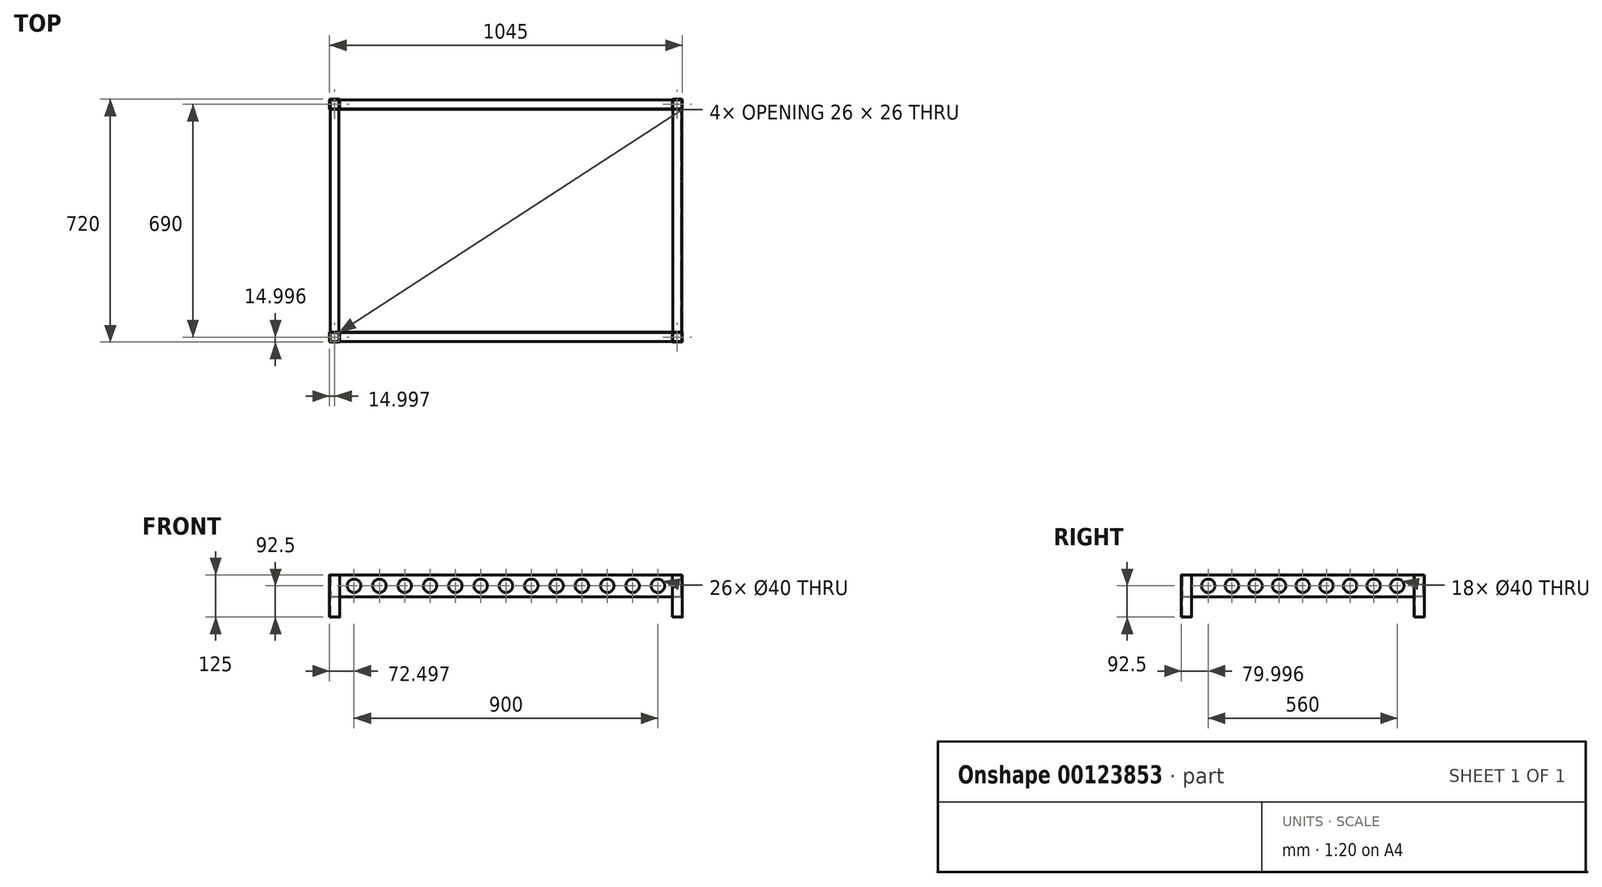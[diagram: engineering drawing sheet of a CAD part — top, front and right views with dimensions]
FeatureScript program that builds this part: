
annotation { "Feature Type Name" : "Feature", "Feature Type Description" : "" }
export const myFeature = defineFeature(function(context is Context, id is Id, definition is map)
    precondition{}
    {
        {
            var Q0;
            Q0=qCreatedBy(makeId("Top.planeOp"),FACE);
            var sketch = newSketch(context, id + "F0", { "sketchPlane" : qUnion([Q0])});
            skLineSegment(sketch, "E0.bottom", {"start": v(-74.45, 26.98) * mm, "end": v(-100.45, 26.98) * mm});
            skLineSegment(sketch, "E0.top", {"start": v(-74.45, 56.98) * mm, "end": v(-100.45, 56.98) * mm});
            skLineSegment(sketch, "E0.left", {"start": v(-72.45, 28.98) * mm, "end": v(-72.45, 54.98) * mm});
            skLineSegment(sketch, "E0.right", {"start": v(-102.45, 28.98) * mm, "end": v(-102.45, 54.98) * mm});
            skPoint(sketch, "E0.middle", {"position": v(-87.45, 41.98) * mm});
            skLineSegment(sketch, "E1.bottom", {"start": v(-75.45, 28.98) * mm, "end": v(-99.45, 28.98) * mm});
            skLineSegment(sketch, "E1.top", {"start": v(-75.45, 54.98) * mm, "end": v(-99.45, 54.98) * mm});
            skLineSegment(sketch, "E1.left", {"start": v(-74.45, 29.98) * mm, "end": v(-74.45, 53.98) * mm});
            skLineSegment(sketch, "E1.right", {"start": v(-100.45, 29.98) * mm, "end": v(-100.45, 53.98) * mm});
            skPoint(sketch, "E2.visualSharp", {"position": v(-102.45, 56.98) * mm});
            skArc(sketch, "E2.filletArc", {"start": v(-100.45, 56.98) * mm, "mid": v(-101.87, 56.39) * mm, "end": v(-102.45, 54.98) * mm});
            skPoint(sketch, "E3.visualSharp", {"position": v(-102.45, 26.98) * mm});
            skArc(sketch, "E3.filletArc", {"start": v(-102.45, 28.98) * mm, "mid": v(-101.87, 27.56) * mm, "end": v(-100.45, 26.98) * mm});
            skPoint(sketch, "E4.visualSharp", {"position": v(-72.45, 26.98) * mm});
            skArc(sketch, "E4.filletArc", {"start": v(-74.45, 26.98) * mm, "mid": v(-73.04, 27.56) * mm, "end": v(-72.45, 28.98) * mm});
            skPoint(sketch, "E5.visualSharp", {"position": v(-72.45, 56.98) * mm});
            skArc(sketch, "E5.filletArc", {"start": v(-72.45, 54.98) * mm, "mid": v(-73.04, 56.39) * mm, "end": v(-74.45, 56.98) * mm});
            skArc(sketch, "E6.filletArc", {"start": v(-74.45, 53.98) * mm, "mid": v(-74.75, 54.68) * mm, "end": v(-75.45, 54.98) * mm});
            skArc(sketch, "E7.filletArc", {"start": v(-99.45, 54.98) * mm, "mid": v(-100.16, 54.68) * mm, "end": v(-100.45, 53.98) * mm});
            skArc(sketch, "E8.filletArc", {"start": v(-100.45, 29.98) * mm, "mid": v(-100.16, 29.27) * mm, "end": v(-99.45, 28.98) * mm});
            skArc(sketch, "E9.filletArc", {"start": v(-75.45, 28.98) * mm, "mid": v(-74.75, 29.27) * mm, "end": v(-74.45, 29.98) * mm});
            skPoint(sketch, "E10.0.1.0", {"position": v(-72.45, -633.02) * mm});
            skPoint(sketch, "E10.0.1.1", {"position": v(-74.45, -635.02) * mm});
            skPoint(sketch, "E10.0.1.2", {"position": v(-74.45, -661.02) * mm});
            skPoint(sketch, "E10.0.1.3", {"position": v(-72.45, -663.02) * mm});
            skPoint(sketch, "E10.0.1.4", {"position": v(-87.45, -648.02) * mm});
            skLineSegment(sketch, "E10.0.1.5", {"start": v(-74.45, -663.02) * mm, "end": v(-100.45, -663.02) * mm});
            skLineSegment(sketch, "E10.0.1.6", {"start": v(-74.45, -633.02) * mm, "end": v(-100.45, -633.02) * mm});
            skPoint(sketch, "E10.0.1.7", {"position": v(-102.45, -663.02) * mm});
            skLineSegment(sketch, "E10.0.1.8", {"start": v(-74.45, -660.02) * mm, "end": v(-74.45, -636.02) * mm});
            skPoint(sketch, "E10.0.1.9", {"position": v(-100.45, -635.02) * mm});
            skArc(sketch, "E10.0.1.10", {"start": v(-100.45, -633.02) * mm, "mid": v(-101.87, -633.61) * mm, "end": v(-102.45, -635.02) * mm});
            skLineSegment(sketch, "E10.0.1.11", {"start": v(-75.45, -635.02) * mm, "end": v(-99.45, -635.02) * mm});
            skLineSegment(sketch, "E10.0.1.12", {"start": v(-72.45, -661.02) * mm, "end": v(-72.45, -635.02) * mm});
            skLineSegment(sketch, "E10.0.1.13", {"start": v(-75.45, -661.02) * mm, "end": v(-99.45, -661.02) * mm});
            skPoint(sketch, "E10.0.1.14", {"position": v(-102.45, -633.02) * mm});
            skLineSegment(sketch, "E10.0.1.15", {"start": v(-102.45, -661.02) * mm, "end": v(-102.45, -635.02) * mm});
            skLineSegment(sketch, "E10.0.1.16", {"start": v(-100.45, -660.02) * mm, "end": v(-100.45, -636.02) * mm});
            skArc(sketch, "E10.0.1.17", {"start": v(-72.45, -635.02) * mm, "mid": v(-73.04, -633.61) * mm, "end": v(-74.45, -633.02) * mm});
            skPoint(sketch, "E10.0.1.18", {"position": v(-100.45, -661.02) * mm});
            skArc(sketch, "E10.0.1.19", {"start": v(-102.45, -661.02) * mm, "mid": v(-101.87, -662.44) * mm, "end": v(-100.45, -663.02) * mm});
            skPoint(sketch, "E10.0.1.20", {"position": v(-87.45, -648.02) * mm});
            skArc(sketch, "E10.0.1.21", {"start": v(-74.45, -663.02) * mm, "mid": v(-73.04, -662.44) * mm, "end": v(-72.45, -661.02) * mm});
            skArc(sketch, "E10.0.1.22", {"start": v(-75.45, -661.02) * mm, "mid": v(-74.75, -660.73) * mm, "end": v(-74.45, -660.02) * mm});
            skArc(sketch, "E10.0.1.23", {"start": v(-100.45, -660.02) * mm, "mid": v(-100.16, -660.73) * mm, "end": v(-99.45, -661.02) * mm});
            skArc(sketch, "E10.0.1.24", {"start": v(-99.45, -635.02) * mm, "mid": v(-100.16, -635.32) * mm, "end": v(-100.45, -636.02) * mm});
            skArc(sketch, "E10.0.1.25", {"start": v(-74.45, -636.02) * mm, "mid": v(-74.75, -635.32) * mm, "end": v(-75.45, -635.02) * mm});
            skPoint(sketch, "E10.1.0.0", {"position": v(942.55, 56.98) * mm});
            skPoint(sketch, "E10.1.0.1", {"position": v(940.55, 54.98) * mm});
            skPoint(sketch, "E10.1.0.2", {"position": v(940.55, 28.98) * mm});
            skPoint(sketch, "E10.1.0.3", {"position": v(942.55, 26.98) * mm});
            skPoint(sketch, "E10.1.0.4", {"position": v(927.55, 41.98) * mm});
            skLineSegment(sketch, "E10.1.0.5", {"start": v(940.55, 26.98) * mm, "end": v(914.55, 26.98) * mm});
            skLineSegment(sketch, "E10.1.0.6", {"start": v(940.55, 56.98) * mm, "end": v(914.55, 56.98) * mm});
            skPoint(sketch, "E10.1.0.7", {"position": v(912.55, 26.98) * mm});
            skLineSegment(sketch, "E10.1.0.8", {"start": v(940.55, 29.98) * mm, "end": v(940.55, 53.98) * mm});
            skPoint(sketch, "E10.1.0.9", {"position": v(914.55, 54.98) * mm});
            skArc(sketch, "E10.1.0.10", {"start": v(914.55, 56.98) * mm, "mid": v(913.13, 56.39) * mm, "end": v(912.55, 54.98) * mm});
            skLineSegment(sketch, "E10.1.0.11", {"start": v(939.55, 54.98) * mm, "end": v(915.55, 54.98) * mm});
            skLineSegment(sketch, "E10.1.0.12", {"start": v(942.55, 28.98) * mm, "end": v(942.55, 54.98) * mm});
            skLineSegment(sketch, "E10.1.0.13", {"start": v(939.55, 28.98) * mm, "end": v(915.55, 28.98) * mm});
            skPoint(sketch, "E10.1.0.14", {"position": v(912.55, 56.98) * mm});
            skLineSegment(sketch, "E10.1.0.15", {"start": v(912.55, 28.98) * mm, "end": v(912.55, 54.98) * mm});
            skLineSegment(sketch, "E10.1.0.16", {"start": v(914.55, 29.98) * mm, "end": v(914.55, 53.98) * mm});
            skArc(sketch, "E10.1.0.17", {"start": v(942.55, 54.98) * mm, "mid": v(941.96, 56.39) * mm, "end": v(940.55, 56.98) * mm});
            skPoint(sketch, "E10.1.0.18", {"position": v(914.55, 28.98) * mm});
            skArc(sketch, "E10.1.0.19", {"start": v(912.55, 28.98) * mm, "mid": v(913.13, 27.56) * mm, "end": v(914.55, 26.98) * mm});
            skPoint(sketch, "E10.1.0.20", {"position": v(927.55, 41.98) * mm});
            skArc(sketch, "E10.1.0.21", {"start": v(940.55, 26.98) * mm, "mid": v(941.96, 27.56) * mm, "end": v(942.55, 28.98) * mm});
            skArc(sketch, "E10.1.0.22", {"start": v(939.55, 28.98) * mm, "mid": v(940.25, 29.27) * mm, "end": v(940.55, 29.98) * mm});
            skArc(sketch, "E10.1.0.23", {"start": v(914.55, 29.98) * mm, "mid": v(914.84, 29.27) * mm, "end": v(915.55, 28.98) * mm});
            skArc(sketch, "E10.1.0.24", {"start": v(915.55, 54.98) * mm, "mid": v(914.84, 54.68) * mm, "end": v(914.55, 53.98) * mm});
            skArc(sketch, "E10.1.0.25", {"start": v(940.55, 53.98) * mm, "mid": v(940.25, 54.68) * mm, "end": v(939.55, 54.98) * mm});
            skPoint(sketch, "E10.1.1.0", {"position": v(942.55, -633.02) * mm});
            skPoint(sketch, "E10.1.1.1", {"position": v(940.55, -635.02) * mm});
            skPoint(sketch, "E10.1.1.2", {"position": v(940.55, -661.02) * mm});
            skPoint(sketch, "E10.1.1.3", {"position": v(942.55, -663.02) * mm});
            skPoint(sketch, "E10.1.1.4", {"position": v(927.55, -648.02) * mm});
            skLineSegment(sketch, "E10.1.1.5", {"start": v(940.55, -663.02) * mm, "end": v(914.55, -663.02) * mm});
            skLineSegment(sketch, "E10.1.1.6", {"start": v(940.55, -633.02) * mm, "end": v(914.55, -633.02) * mm});
            skPoint(sketch, "E10.1.1.7", {"position": v(912.55, -663.02) * mm});
            skLineSegment(sketch, "E10.1.1.8", {"start": v(940.55, -660.02) * mm, "end": v(940.55, -636.02) * mm});
            skPoint(sketch, "E10.1.1.9", {"position": v(914.55, -635.02) * mm});
            skArc(sketch, "E10.1.1.10", {"start": v(914.55, -633.02) * mm, "mid": v(913.13, -633.61) * mm, "end": v(912.55, -635.02) * mm});
            skLineSegment(sketch, "E10.1.1.11", {"start": v(939.55, -635.02) * mm, "end": v(915.55, -635.02) * mm});
            skLineSegment(sketch, "E10.1.1.12", {"start": v(942.55, -661.02) * mm, "end": v(942.55, -635.02) * mm});
            skLineSegment(sketch, "E10.1.1.13", {"start": v(939.55, -661.02) * mm, "end": v(915.55, -661.02) * mm});
            skPoint(sketch, "E10.1.1.14", {"position": v(912.55, -633.02) * mm});
            skLineSegment(sketch, "E10.1.1.15", {"start": v(912.55, -661.02) * mm, "end": v(912.55, -635.02) * mm});
            skLineSegment(sketch, "E10.1.1.16", {"start": v(914.55, -660.02) * mm, "end": v(914.55, -636.02) * mm});
            skArc(sketch, "E10.1.1.17", {"start": v(942.55, -635.02) * mm, "mid": v(941.96, -633.61) * mm, "end": v(940.55, -633.02) * mm});
            skPoint(sketch, "E10.1.1.18", {"position": v(914.55, -661.02) * mm});
            skArc(sketch, "E10.1.1.19", {"start": v(912.55, -661.02) * mm, "mid": v(913.13, -662.44) * mm, "end": v(914.55, -663.02) * mm});
            skPoint(sketch, "E10.1.1.20", {"position": v(927.55, -648.02) * mm});
            skArc(sketch, "E10.1.1.21", {"start": v(940.55, -663.02) * mm, "mid": v(941.96, -662.44) * mm, "end": v(942.55, -661.02) * mm});
            skArc(sketch, "E10.1.1.22", {"start": v(939.55, -661.02) * mm, "mid": v(940.25, -660.73) * mm, "end": v(940.55, -660.02) * mm});
            skArc(sketch, "E10.1.1.23", {"start": v(914.55, -660.02) * mm, "mid": v(914.84, -660.73) * mm, "end": v(915.55, -661.02) * mm});
            skArc(sketch, "E10.1.1.24", {"start": v(915.55, -635.02) * mm, "mid": v(914.84, -635.32) * mm, "end": v(914.55, -636.02) * mm});
            skArc(sketch, "E10.1.1.25", {"start": v(940.55, -636.02) * mm, "mid": v(940.25, -635.32) * mm, "end": v(939.55, -635.02) * mm});
            skLineSegment(sketch, "E10.direction1", {"start": v(-102.45, 26.98) * mm, "end": v(912.55, 26.98) * mm, "construction": true});
            skLineSegment(sketch, "E10.direction2", {"start": v(-102.45, 26.98) * mm, "end": v(-102.45, -663.02) * mm, "construction": true});
            skSolve(sketch);
        }
        {
            var Q0;
            Q0=makeQuery(id+"F0.imprint","IMPRINT",FACE,{"disambiguationData":[TD([[makeQuery(id+"F0.imprint","IMPRINT",EDGE,{"derivedFrom":sQuery(id+"F0.wireOp",EDGE,"E0.bottom")}),-1.0]])]});
            var Q1;
            Q1=makeQuery(id+"F0.imprint","IMPRINT",FACE,{"disambiguationData":[TD([[makeQuery(id+"F0.imprint","IMPRINT",EDGE,{"derivedFrom":sQuery(id+"F0.wireOp",EDGE,"E10.0.1.5")}),-1.0]])]});
            var Q2;
            Q2=makeQuery(id+"F0.imprint","IMPRINT",FACE,{"disambiguationData":[TD([[makeQuery(id+"F0.imprint","IMPRINT",EDGE,{"derivedFrom":sQuery(id+"F0.wireOp",EDGE,"E10.1.1.5")}),-1.0]])]});
            var Q3;
            Q3=makeQuery(id+"F0.imprint","IMPRINT",FACE,{"disambiguationData":[TD([[makeQuery(id+"F0.imprint","IMPRINT",EDGE,{"derivedFrom":sQuery(id+"F0.wireOp",EDGE,"E10.1.0.5")}),-1.0]])]});
            extrude(context, id + "F1", {"entities" : qUnion([Q0, Q1, Q2, Q3]), "depth" : 125 * mm});
        }
        {
            var Q0;
            Q0=makeQuery(id+"F1.opExtrude","SWEPT_FACE",FACE,{"disambiguationData":[OSD([sQuery(id+"F0.wireOp",EDGE,"E0.bottom")])]});
            var sketch = newSketch(context, id + "F2", { "sketchPlane" : qUnion([Q0])});
            skLineSegment(sketch, "E11", {"start": v(-74.45, 125) * mm, "end": v(-99.45, 125) * mm});
            skLineSegment(sketch, "E12", {"start": v(-100.45, 124) * mm, "end": v(-100.45, 61) * mm});
            skLineSegment(sketch, "E13", {"start": v(-99.45, 60) * mm, "end": v(939.55, 60) * mm});
            skLineSegment(sketch, "E14", {"start": v(940.55, 61) * mm, "end": v(940.55, 124) * mm});
            skLineSegment(sketch, "E15", {"start": v(939.55, 125) * mm, "end": v(914.55, 125) * mm});
            skLineSegment(sketch, "E16.0", {"start": v(938.55, 123.5) * mm, "end": v(914.55, 123.5) * mm});
            skLineSegment(sketch, "E16.1", {"start": v(-74.45, 123.5) * mm, "end": v(-98.45, 123.5) * mm});
            skLineSegment(sketch, "E16.2", {"start": v(-98.95, 123) * mm, "end": v(-98.95, 62) * mm});
            skLineSegment(sketch, "E16.3", {"start": v(-98.45, 61.5) * mm, "end": v(938.55, 61.5) * mm});
            skLineSegment(sketch, "E16.4", {"start": v(939.05, 62) * mm, "end": v(939.05, 123) * mm});
            skLineSegment(sketch, "E17", {"start": v(-74.45, 125) * mm, "end": v(-74.45, 123.5) * mm});
            skLineSegment(sketch, "E18", {"start": v(914.55, 125) * mm, "end": v(914.55, 123.5) * mm});
            skPoint(sketch, "E19.visualSharp", {"position": v(940.55, 125) * mm});
            skArc(sketch, "E19.filletArc", {"start": v(940.55, 124) * mm, "mid": v(940.25, 124.7) * mm, "end": v(939.55, 125) * mm});
            skPoint(sketch, "E20.visualSharp", {"position": v(940.55, 60) * mm});
            skArc(sketch, "E20.filletArc", {"start": v(939.55, 60) * mm, "mid": v(940.25, 60.3) * mm, "end": v(940.55, 61) * mm});
            skPoint(sketch, "E21.visualSharp", {"position": v(-100.45, 60) * mm});
            skArc(sketch, "E21.filletArc", {"start": v(-100.45, 61) * mm, "mid": v(-100.16, 60.3) * mm, "end": v(-99.45, 60) * mm});
            skPoint(sketch, "E22.visualSharp", {"position": v(-100.45, 125) * mm});
            skArc(sketch, "E22.filletArc", {"start": v(-99.45, 125) * mm, "mid": v(-100.16, 124.7) * mm, "end": v(-100.45, 124) * mm});
            skPoint(sketch, "E23.visualSharp", {"position": v(-98.95, 123.5) * mm});
            skArc(sketch, "E23.filletArc", {"start": v(-98.45, 123.5) * mm, "mid": v(-98.8, 123.35) * mm, "end": v(-98.95, 123) * mm});
            skPoint(sketch, "E24.visualSharp", {"position": v(-98.95, 61.5) * mm});
            skArc(sketch, "E24.filletArc", {"start": v(-98.95, 62) * mm, "mid": v(-98.8, 61.65) * mm, "end": v(-98.45, 61.5) * mm});
            skPoint(sketch, "E25.visualSharp", {"position": v(939.05, 123.5) * mm});
            skArc(sketch, "E25.filletArc", {"start": v(939.05, 123) * mm, "mid": v(938.9, 123.35) * mm, "end": v(938.55, 123.5) * mm});
            skPoint(sketch, "E26.visualSharp", {"position": v(939.05, 61.5) * mm});
            skArc(sketch, "E26.filletArc", {"start": v(938.55, 61.5) * mm, "mid": v(938.9, 61.65) * mm, "end": v(939.05, 62) * mm});
            skSolve(sketch);
        }
        {
            var Q0;
            Q0 = qSketchRegion(id + "F2", true);
            var Q1;
            Q1=makeQuery(id+"F1.opExtrude","SWEPT_FACE",FACE,{"disambiguationData":[OSD([sQuery(id+"F0.wireOp",EDGE,"E10.0.1.6")])]});
            extrude(context, id + "F3", {"entities" : qUnion([Q0]), "endBound" : BoundingType.UP_TO_SURFACE, "endBoundEntityFace" : qUnion([Q1]), "depth" : 495.87 * mm});
        }
        {
            var Q0;
            Q0=makeQuery(id+"F1.opExtrude","SWEPT_FACE",FACE,{"disambiguationData":[OSD([sQuery(id+"F0.wireOp",EDGE,"E10.1.1.15")])]});
            var sketch = newSketch(context, id + "F4", { "sketchPlane" : qUnion([Q0])});
            skLineSegment(sketch, "E27", {"start": v(635.02, 125) * mm, "end": v(660.02, 125) * mm});
            skLineSegment(sketch, "E28", {"start": v(661.02, 124) * mm, "end": v(661.02, 61) * mm});
            skLineSegment(sketch, "E29", {"start": v(660.02, 60) * mm, "end": v(633.02, 60) * mm});
            skLineSegment(sketch, "E30.0", {"start": v(659.02, 61.5) * mm, "end": v(633.02, 61.5) * mm});
            skLineSegment(sketch, "E30.1", {"start": v(659.52, 123) * mm, "end": v(659.52, 62) * mm});
            skLineSegment(sketch, "E30.2", {"start": v(635.02, 123.5) * mm, "end": v(659.02, 123.5) * mm});
            skLineSegment(sketch, "E31", {"start": v(635.02, 125) * mm, "end": v(635.02, 123.5) * mm});
            skLineSegment(sketch, "E32", {"start": v(633.02, 61.5) * mm, "end": v(633.02, 60) * mm});
            skPoint(sketch, "E33.visualSharp", {"position": v(661.02, 125) * mm});
            skArc(sketch, "E33.filletArc", {"start": v(661.02, 124) * mm, "mid": v(660.73, 124.7) * mm, "end": v(660.02, 125) * mm});
            skPoint(sketch, "E34.visualSharp", {"position": v(661.02, 60) * mm});
            skArc(sketch, "E34.filletArc", {"start": v(660.02, 60) * mm, "mid": v(660.73, 60.3) * mm, "end": v(661.02, 61) * mm});
            skPoint(sketch, "E35.visualSharp", {"position": v(659.52, 123.5) * mm});
            skArc(sketch, "E35.filletArc", {"start": v(659.52, 123) * mm, "mid": v(659.38, 123.35) * mm, "end": v(659.02, 123.5) * mm});
            skPoint(sketch, "E36.visualSharp", {"position": v(659.52, 61.5) * mm});
            skArc(sketch, "E36.filletArc", {"start": v(659.02, 61.5) * mm, "mid": v(659.38, 61.65) * mm, "end": v(659.52, 62) * mm});
            skSolve(sketch);
        }
        {
            var Q0;
            Q0 = qSketchRegion(id + "F4", true);
            var Q1;
            Q1=makeQuery(id+"F1.opExtrude","SWEPT_FACE",FACE,{"disambiguationData":[OSD([sQuery(id+"F0.wireOp",EDGE,"E10.0.1.12")])]});
            extrude(context, id + "F5", {"entities" : qUnion([Q0]), "endBound" : BoundingType.UP_TO_SURFACE, "endBoundEntityFace" : qUnion([Q1]), "depth" : 25 * mm});
        }
        {
            var Q0;
            Q0=makeQuery(id+"F1.opExtrude","SWEPT_FACE",FACE,{"disambiguationData":[OSD([sQuery(id+"F0.wireOp",EDGE,"E10.1.0.15")])]});
            var sketch = newSketch(context, id + "F6", { "sketchPlane" : qUnion([Q0])});
            skLineSegment(sketch, "E37", {"start": v(-28.98, 125) * mm, "end": v(-53.98, 125) * mm});
            skLineSegment(sketch, "E38", {"start": v(-54.98, 124) * mm, "end": v(-54.98, 61) * mm});
            skLineSegment(sketch, "E39", {"start": v(-53.98, 60) * mm, "end": v(-26.98, 60) * mm});
            skLineSegment(sketch, "E40.0", {"start": v(-52.98, 61.5) * mm, "end": v(-26.98, 61.5) * mm});
            skLineSegment(sketch, "E40.1", {"start": v(-53.48, 123) * mm, "end": v(-53.48, 62) * mm});
            skLineSegment(sketch, "E40.2", {"start": v(-28.98, 123.5) * mm, "end": v(-52.98, 123.5) * mm});
            skLineSegment(sketch, "E41", {"start": v(-28.98, 125) * mm, "end": v(-28.98, 123.5) * mm});
            skLineSegment(sketch, "E42", {"start": v(-26.98, 61.5) * mm, "end": v(-26.98, 60) * mm});
            skPoint(sketch, "E43.visualSharp", {"position": v(-54.98, 125) * mm});
            skArc(sketch, "E43.filletArc", {"start": v(-53.98, 125) * mm, "mid": v(-54.68, 124.7) * mm, "end": v(-54.98, 124) * mm});
            skPoint(sketch, "E44.visualSharp", {"position": v(-54.98, 60) * mm});
            skArc(sketch, "E44.filletArc", {"start": v(-54.98, 61) * mm, "mid": v(-54.68, 60.3) * mm, "end": v(-53.98, 60) * mm});
            skPoint(sketch, "E45.visualSharp", {"position": v(-53.48, 61.5) * mm});
            skArc(sketch, "E45.filletArc", {"start": v(-53.48, 62) * mm, "mid": v(-53.33, 61.65) * mm, "end": v(-52.98, 61.5) * mm});
            skPoint(sketch, "E46.visualSharp", {"position": v(-53.48, 123.5) * mm});
            skArc(sketch, "E46.filletArc", {"start": v(-52.98, 123.5) * mm, "mid": v(-53.33, 123.35) * mm, "end": v(-53.48, 123) * mm});
            skSolve(sketch);
        }
        {
            var Q0;
            Q0 = qSketchRegion(id + "F6", true);
            var Q1;
            Q1=makeQuery(id+"F1.opExtrude","SWEPT_FACE",FACE,{"disambiguationData":[OSD([sQuery(id+"F0.wireOp",EDGE,"E0.left")])]});
            extrude(context, id + "F7", {"entities" : qUnion([Q0]), "endBound" : BoundingType.UP_TO_SURFACE, "endBoundEntityFace" : qUnion([Q1]), "depth" : 25 * mm});
        }
        {
            var Q0;
            Q0=makeQuery(id+"F3.opExtrude","SWEPT_FACE",FACE,{"disambiguationData":[OSD([sQuery(id+"F2.wireOp",EDGE,"E12")])]});
            var sketch = newSketch(context, id + "F8", { "sketchPlane" : qUnion([Q0])});
            skCircle(sketch, "E47", {"center": v(303.02, 92.5) * mm, "radius": 20 * mm});
            skPoint(sketch, "E47.centerSnap0", {"position": v(303.02, 61) * mm});
            skPoint(sketch, "E47.centerSnap1", {"position": v(-26.98, 92.5) * mm});
            skCircle(sketch, "E48.1.0.0", {"center": v(373.02, 92.5) * mm, "radius": 20 * mm});
            skCircle(sketch, "E48.2.0.0", {"center": v(443.02, 92.5) * mm, "radius": 20 * mm});
            skCircle(sketch, "E48.3.0.0", {"center": v(513.02, 92.5) * mm, "radius": 20 * mm});
            skCircle(sketch, "E48.4.0.0", {"center": v(583.02, 92.5) * mm, "radius": 20 * mm});
            skLineSegment(sketch, "E48.direction1", {"start": v(303.02, 92.5) * mm, "end": v(373.02, 92.5) * mm, "construction": true});
            skLineSegment(sketch, "E49", {"start": v(303.02, 92.5) * mm, "end": v(303.02, 140.48) * mm, "construction": true});
            skLineSegment(sketch, "E50.MirrorCS", {"start": v(303.02, 92.5) * mm, "end": v(303.02, 44.52) * mm, "construction": true});
            skCircle(sketch, "E51.MirrorC", {"center": v(163.02, 92.5) * mm, "radius": 20 * mm});
            skCircle(sketch, "E52.MirrorC", {"center": v(93.02, 92.5) * mm, "radius": 20 * mm});
            skCircle(sketch, "E53.MirrorC", {"center": v(23.02, 92.5) * mm, "radius": 20 * mm});
            skCircle(sketch, "E54.MirrorC", {"center": v(233.02, 92.5) * mm, "radius": 20 * mm});
            skLineSegment(sketch, "E55.MirrorCS", {"start": v(303.02, 92.5) * mm, "end": v(233.02, 92.5) * mm, "construction": true});
            skSolve(sketch);
        }
        {
            var Q0;
            Q0 = qSketchRegion(id + "F8", true);
            extrude(context, id + "F9", {"entities" : qUnion([Q0]), "operationType" : NewBodyOperationType.REMOVE, "endBound" : BoundingType.THROUGH_ALL, "oppositeDirection" : true, "depth" : 25 * mm});
        }
        {
            var Q0;
            Q0=makeQuery(id+"F7.opExtrude","SWEPT_FACE",FACE,{"disambiguationData":[OSD([sQuery(id+"F6.wireOp",EDGE,"E38")])]});
            var sketch = newSketch(context, id + "F10", { "sketchPlane" : qUnion([Q0])});
            skCircle(sketch, "E56", {"center": v(-420.05, 92.5) * mm, "radius": 20 * mm});
            skPoint(sketch, "E56.centerSnap0", {"position": v(-420.05, 61) * mm});
            skPoint(sketch, "E56.centerSnap1", {"position": v(-912.55, 92.5) * mm});
            skCircle(sketch, "E57.1.0.0", {"center": v(-345.05, 92.5) * mm, "radius": 20 * mm});
            skCircle(sketch, "E57.2.0.0", {"center": v(-270.05, 92.5) * mm, "radius": 20 * mm});
            skCircle(sketch, "E57.3.0.0", {"center": v(-195.05, 92.5) * mm, "radius": 20 * mm});
            skCircle(sketch, "E57.4.0.0", {"center": v(-120.05, 92.5) * mm, "radius": 20 * mm});
            skCircle(sketch, "E57.5.0.0", {"center": v(-45.05, 92.5) * mm, "radius": 20 * mm});
            skCircle(sketch, "E57.6.0.0", {"center": v(29.95, 92.5) * mm, "radius": 20 * mm});
            skLineSegment(sketch, "E57.direction1", {"start": v(-420.05, 92.5) * mm, "end": v(-345.05, 92.5) * mm, "construction": true});
            skLineSegment(sketch, "E58", {"start": v(-420.05, 92.5) * mm, "end": v(-420.05, 179.89) * mm, "construction": true});
            skCircle(sketch, "E59.MirrorC", {"center": v(-645.05, 92.5) * mm, "radius": 20 * mm});
            skCircle(sketch, "E60.MirrorC", {"center": v(-570.05, 92.5) * mm, "radius": 20 * mm});
            skCircle(sketch, "E61.MirrorC", {"center": v(-495.05, 92.5) * mm, "radius": 20 * mm});
            skLineSegment(sketch, "E62.MirrorCS", {"start": v(-420.05, 92.5) * mm, "end": v(-495.05, 92.5) * mm, "construction": true});
            skCircle(sketch, "E63.MirrorC", {"center": v(-720.05, 92.5) * mm, "radius": 20 * mm});
            skCircle(sketch, "E64.MirrorC", {"center": v(-870.05, 92.5) * mm, "radius": 20 * mm});
            skCircle(sketch, "E65.MirrorC", {"center": v(-795.05, 92.5) * mm, "radius": 20 * mm});
            skSolve(sketch);
        }
        {
            var Q0;
            Q0 = qSketchRegion(id + "F10", true);
            extrude(context, id + "F11", {"entities" : qUnion([Q0]), "operationType" : NewBodyOperationType.REMOVE, "endBound" : BoundingType.THROUGH_ALL, "oppositeDirection" : true, "depth" : 783.85 * mm});
        }
    });
